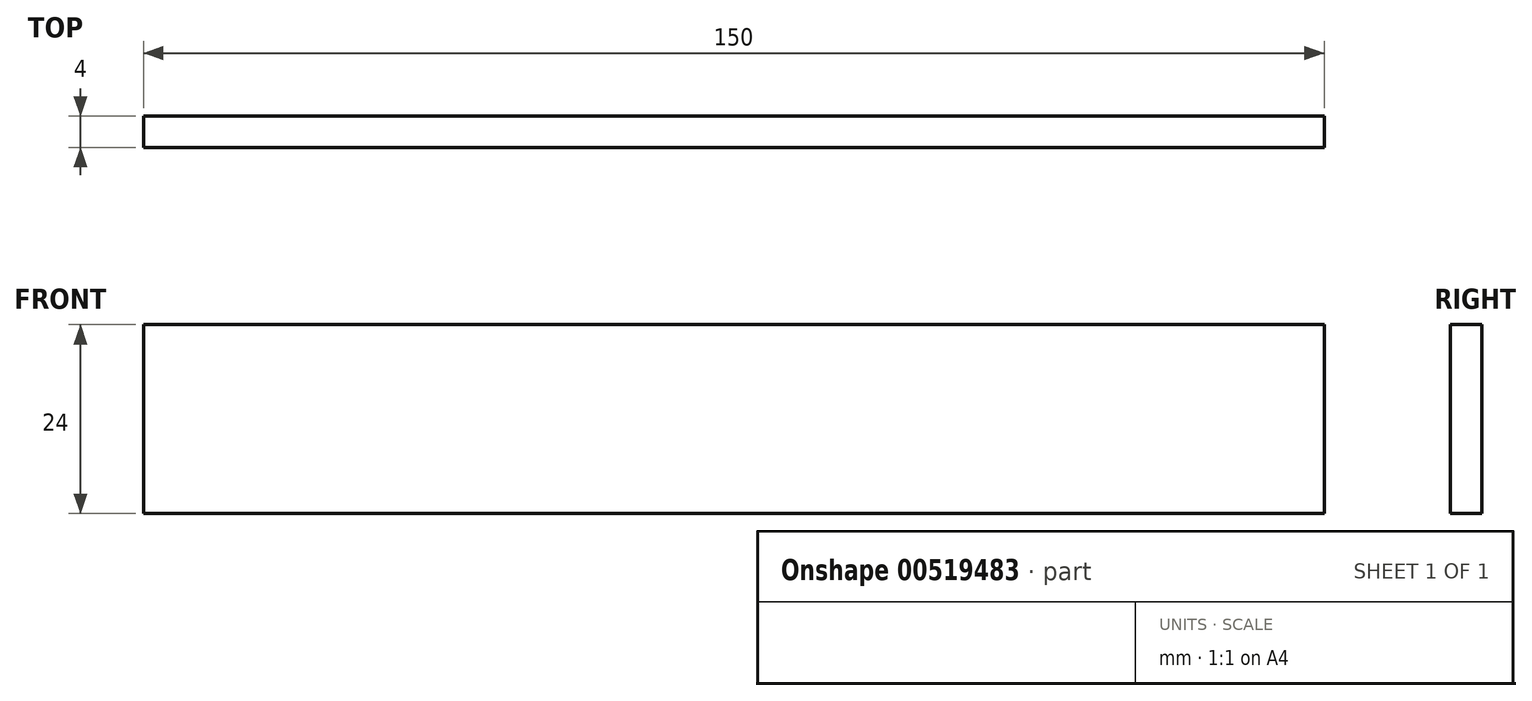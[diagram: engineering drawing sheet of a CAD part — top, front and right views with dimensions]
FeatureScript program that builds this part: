
annotation { "Feature Type Name" : "Feature", "Feature Type Description" : "" }
export const myFeature = defineFeature(function(context is Context, id is Id, definition is map)
    precondition{}
    {
        {
            var Q0;
            Q0=qCreatedBy(makeId("Front.planeOp"),FACE);
            var sketch = newSketch(context, id + "F0", { "sketchPlane" : qUnion([Q0])});
            skLineSegment(sketch, "E0.bottom", {"start": v(0, 0) * mm, "end": v(150, 0) * mm});
            skLineSegment(sketch, "E0.top", {"start": v(0, 24) * mm, "end": v(150, 24) * mm});
            skLineSegment(sketch, "E0.left", {"start": v(0, 0) * mm, "end": v(0, 24) * mm});
            skLineSegment(sketch, "E0.right", {"start": v(150, 0) * mm, "end": v(150, 24) * mm});
            skSolve(sketch);
        }
        {
            var Q0;
            Q0=makeQuery(id+"F0.imprint","IMPRINT",FACE,{"disambiguationData":[TD([[makeQuery(id+"F0.imprint","IMPRINT",EDGE,{"derivedFrom":sQuery(id+"F0.wireOp",EDGE,"E0.bottom")}),1.0]])]});
            extrude(context, id + "F1", {"entities" : qUnion([Q0]), "depth" : 4 * mm, "offsetDistance" : 25 * mm});
        }
    });
